# Revit family: Specialty_Equipment-Detroit_Radiant-Unit_Heater-FA_Series-rev
name_source: partatom
category: Specialty Equipment
units: mm (PartAtom-declared; Revit-internal decimal feet)

## family parameters
Always vertical = Yes
Cut with Voids When Loaded = No
Enable Cutting in Views = No
Maintain Annotation Orientation = No
OmniClass Number = 23.75.00.00
OmniClass Title = Climate Control (HVAC)
Part Type = Normal
Room Calculation Point = No
Round Connector Dimension = Use Diameter
Shared = No
Work Plane-Based = No

## types (9) — shared parameters
Assembly Code = D3020
CD_Finish = Metal-Steel-Detroit_Radiant-Coated_Aluminized_Steel
CD_Finish Component = Metal-Steel-Detroit_Radiant-Stainless
CD_Heater Depth = 1' - 8"
CD_Install Documentation = https://www.reverberray.com
CD_Louver Spacing = 0' - 3"
CD_Microsite = https://www.caddetails.com
CD_Mounting Hole Offset Side = 0' - 6"
CD_Mounting Hole Spacing Depth = 0' - 9 1/2"
CD_Product Documentation Link = https://www.reverberray.com
CD_Product Name = Gas-Fired, Induced Draft, Hot Air Unit Heaters
CD_Product Page URL = https://www.reverberray.com
CD_Requested Rod Bottom Height = 0' - 0"
CD_Requested Rod Top Height = 1' - 0"
CD_Threaded Rod Height Bottom = 0' - 0"
CD_Unit Size = Description of Product Sizing, set with equation if possible
Description = Gas-Fired, Induced Draft, Hot Air Unit Heaters
Manufacturer = Detroit Radiant Products Company
URL = https://www.reverberray.com

## per-type parameters (varying)
- FA-100: 100_125=Yes; 150_200=No; 225_250=No; 300=No; 400=No; CD_Fan Depth=0' - 4 1/2"; CD_Fan Offset W=1' - 1"; CD_Fan Radius=0' - 9"; CD_Gas Connector=100,000 BTU; CD_Gas Offset H=1' - 7"; CD_Gas Offset W=0' - 5"; CD_Heater Height=1' - 9"; CD_Heater Width=3' - 4"; CD_Louver W=2' - 2 1/2"; CD_Motor Depth=0' - 9 1/2"; CD_Mounting Hole Spacing Width=1' - 7"; CD_Number of Louvers=7; CD_Vent Diameter=0' - 4"; CD_Vent Offset H=0' - 4"; CD_Vent Offset W=0' - 6"; CD_Vent Radius=0' - 2"; CD_Void Offset Left=0' - 1"; CD_Void Offset Right=1' - 0 1/2"; Default Elevation=12' - 0"; Threaded Rod=No
- FA-125: 100_125=Yes; 150_200=No; 225_250=No; 300=No; 400=No; CD_Fan Depth=0' - 4 1/2"; CD_Fan Offset W=1' - 1"; CD_Fan Radius=0' - 9"; CD_Gas Connector=125,000 BTU; CD_Gas Offset H=1' - 7"; CD_Gas Offset W=0' - 5"; CD_Heater Height=1' - 9"; CD_Heater Width=3' - 4"; CD_Louver W=2' - 2 1/2"; CD_Motor Depth=0' - 9 1/2"; CD_Mounting Hole Spacing Width=1' - 7"; CD_Number of Louvers=7; CD_Vent Diameter=0' - 4"; CD_Vent Offset H=0' - 4"; CD_Vent Offset W=0' - 6"; CD_Vent Radius=0' - 2"; CD_Void Offset Left=0' - 1"; CD_Void Offset Right=1' - 0 1/2"; Default Elevation=14' - 0"; Threaded Rod=Yes
- FA-150: 100_125=No; 150_200=Yes; 225_250=No; 300=No; 400=No; CD_Fan Depth=0' - 4 1/2"; CD_Fan Offset W=1' - 1"; CD_Fan Radius=0' - 11"; CD_Gas Connector=150,000 BTU; CD_Gas Offset H=2' - 1"; CD_Gas Offset W=0' - 5"; CD_Heater Height=2' - 3"; CD_Heater Width=3' - 4"; CD_Louver W=2' - 2 1/2"; CD_Motor Depth=0' - 9 1/2"; CD_Mounting Hole Spacing Width=1' - 7"; CD_Number of Louvers=9; CD_Vent Diameter=0' - 6"; CD_Vent Offset H=0' - 4"; CD_Vent Offset W=0' - 6"; CD_Vent Radius=0' - 3"; CD_Void Offset Left=0' - 1"; CD_Void Offset Right=1' - 0 1/2"; Default Elevation=14' - 0"; Threaded Rod=Yes
- FA-175: 100_125=No; 150_200=Yes; 225_250=No; 300=No; 400=No; CD_Fan Depth=0' - 4 1/2"; CD_Fan Offset W=1' - 1"; CD_Fan Radius=0' - 11"; CD_Gas Connector=175,000 BTU; CD_Gas Offset H=2' - 1"; CD_Gas Offset W=0' - 5"; CD_Heater Height=2' - 3"; CD_Heater Width=3' - 4"; CD_Louver W=2' - 2 1/2"; CD_Motor Depth=0' - 9 1/2"; CD_Mounting Hole Spacing Width=1' - 7"; CD_Number of Louvers=9; CD_Vent Diameter=0' - 6"; CD_Vent Offset H=0' - 4"; CD_Vent Offset W=0' - 6"; CD_Vent Radius=0' - 3"; CD_Void Offset Left=0' - 1"; CD_Void Offset Right=1' - 0 1/2"; Default Elevation=15' - 0"; Threaded Rod=Yes
- FA-200: 100_125=No; 150_200=Yes; 225_250=No; 300=No; 400=No; CD_Fan Depth=0' - 4 1/2"; CD_Fan Offset W=1' - 1"; CD_Fan Radius=0' - 11"; CD_Gas Connector=200,000 BTU; CD_Gas Offset H=2' - 1"; CD_Gas Offset W=0' - 5"; CD_Heater Height=2' - 3"; CD_Heater Width=3' - 4"; CD_Louver W=2' - 2 1/2"; CD_Motor Depth=0' - 9 1/2"; CD_Mounting Hole Spacing Width=1' - 7"; CD_Number of Louvers=9; CD_Vent Diameter=0' - 6"; CD_Vent Offset H=0' - 4"; CD_Vent Offset W=0' - 6"; CD_Vent Radius=0' - 3"; CD_Void Offset Left=0' - 1"; CD_Void Offset Right=1' - 0 1/2"; Default Elevation=15' - 0"; Threaded Rod=Yes
- FA-225: 100_125=No; 150_200=No; 225_250=Yes; 300=No; 400=No; CD_Fan Depth=0' - 4 1/2"; CD_Fan Offset W=1' - 1"; CD_Fan Radius=0' - 11"; CD_Gas Connector=225,000 BTU; CD_Gas Offset H=0' - 11"; CD_Gas Offset W=0' - 5"; CD_Heater Height=2' - 6"; CD_Heater Width=3' - 4"; CD_Louver W=2' - 2 1/2"; CD_Motor Depth=0' - 9 1/2"; CD_Mounting Hole Spacing Width=1' - 7"; CD_Number of Louvers=9; CD_Vent Diameter=0' - 6"; CD_Vent Offset H=0' - 4"; CD_Vent Offset W=0' - 6"; CD_Vent Radius=0' - 3"; CD_Void Offset Left=0' - 1"; CD_Void Offset Right=1' - 0 1/2"; Default Elevation=16' - 0"; Threaded Rod=Yes
- FA-250: 100_125=No; 150_200=No; 225_250=Yes; 300=No; 400=No; CD_Fan Depth=0' - 4 1/2"; CD_Fan Offset W=1' - 1"; CD_Fan Radius=0' - 11"; CD_Gas Connector=250,000 BTU; CD_Gas Offset H=0' - 11"; CD_Gas Offset W=0' - 5"; CD_Heater Height=2' - 6"; CD_Heater Width=3' - 4"; CD_Louver W=2' - 2 1/2"; CD_Motor Depth=0' - 9 1/2"; CD_Mounting Hole Spacing Width=1' - 7"; CD_Number of Louvers=9; CD_Vent Diameter=0' - 6"; CD_Vent Offset H=0' - 4"; CD_Vent Offset W=0' - 6"; CD_Vent Radius=0' - 3"; CD_Void Offset Left=0' - 1"; CD_Void Offset Right=1' - 0 1/2"; Default Elevation=16' - 0"; Threaded Rod=Yes
- FA-300: 100_125=No; 150_200=No; 225_250=No; 300=Yes; 400=No; CD_Fan Depth=0' - 6 1/2"; CD_Fan Offset W=2' - 8 1/2"; CD_Fan Radius=1' - 1"; CD_Gas Connector=300,000 BTU; CD_Gas Offset H=1' - 11 1/2"; CD_Gas Offset W=3' - 6"; CD_Heater Height=3' - 0"; CD_Heater Width=4' - 2"; CD_Louver W=2' - 9"; CD_Motor Depth=1' - 0"; CD_Mounting Hole Spacing Width=2' - 2"; CD_Number of Louvers=12; CD_Vent Diameter=0' - 6"; CD_Vent Offset H=2' - 7 1/2"; CD_Vent Offset W=3' - 8 1/2"; CD_Vent Radius=0' - 3"; CD_Void Offset Left=1' - 4"; CD_Void Offset Right=0' - 1"; Default Elevation=18' - 0"; Threaded Rod=No
- FA-400: 100_125=No; 150_200=No; 225_250=No; 300=No; 400=Yes; CD_Fan Depth=0' - 3 1/2"; CD_Fan Offset W=1' - 7 1/2"; CD_Fan Radius=1' - 3"; CD_Gas Connector=400,000 BTU; CD_Gas Offset H=1' - 2"; CD_Gas Offset W=0' - 8 1/2"; CD_Heater Height=3' - 8"; CD_Heater Width=4' - 6"; CD_Louver W=3' - 1"; CD_Motor Depth=0' - 10 1/2"; CD_Mounting Hole Spacing Width=2' - 5 1/2"; CD_Number of Louvers=15; CD_Vent Diameter=0' - 6"; CD_Vent Offset H=0' - 4"; CD_Vent Offset W=0' - 6"; CD_Vent Radius=0' - 3"; CD_Void Offset Left=0' - 1"; CD_Void Offset Right=1' - 4"; Default Elevation=20' - 0"; Threaded Rod=Yes

note: column(s) folded — value = type name in every type: Model

## geometry (parser evidence)
native form markers: Sweep x4
no freeform markers — native parametric forms only
